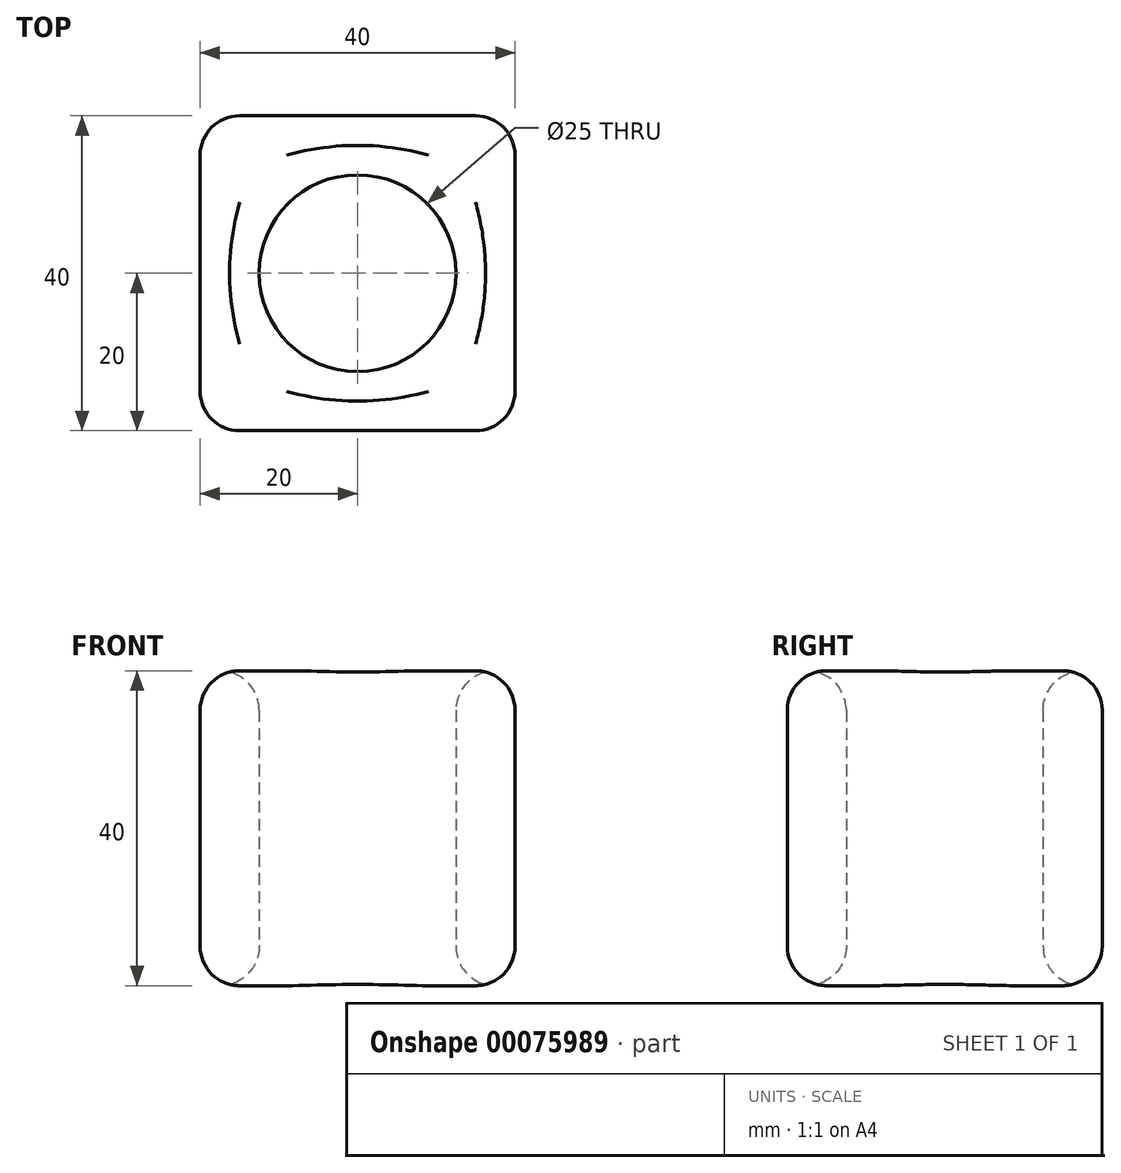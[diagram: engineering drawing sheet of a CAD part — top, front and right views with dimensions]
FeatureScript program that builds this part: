
annotation { "Feature Type Name" : "Feature", "Feature Type Description" : "" }
export const myFeature = defineFeature(function(context is Context, id is Id, definition is map)
    precondition{}
    {
        {
            var Q0;
            Q0=qCreatedBy(makeId("Top.planeOp"),FACE);
            var sketch = newSketch(context, id + "F0", { "sketchPlane" : qUnion([Q0])});
            skLineSegment(sketch, "E0.bottom", {"start": v(20, 20) * mm, "end": v(-20, 20) * mm});
            skLineSegment(sketch, "E0.top", {"start": v(20, -20) * mm, "end": v(-20, -20) * mm});
            skLineSegment(sketch, "E0.left", {"start": v(20, 20) * mm, "end": v(20, -20) * mm});
            skLineSegment(sketch, "E0.right", {"start": v(-20, 20) * mm, "end": v(-20, -20) * mm});
            skPoint(sketch, "E0.middle", {"position": v(0, 0) * mm});
            skCircle(sketch, "E1", {"center": v(0, 0) * mm, "radius": 12.5 * mm});
            skSolve(sketch);
        }
        {
            var Q0;
            Q0=makeQuery(id+"F0.imprint","IMPRINT",FACE,{"disambiguationData":[TD([[makeQuery(id+"F0.imprint","IMPRINT",EDGE,{"derivedFrom":sQuery(id+"F0.wireOp",EDGE,"E0.bottom")}),1.0]])]});
            extrude(context, id + "F1", {"entities" : qUnion([Q0]), "depth" : 20 * mm, "hasSecondDirection" : true, "secondDirectionOppositeDirection" : true, "secondDirectionDepth" : 20 * mm});
        }
        {
            var Q0;
            Q0=makeQuery(id+"F1.opExtrude","CAP_FACE",FACE,{"disambiguationData":[OSD([sQuery(id+"F0.wireOp",EDGE,"E0.bottom"),sQuery(id+"F0.wireOp",EDGE,"E0.top"),sQuery(id+"F0.wireOp",EDGE,"E0.left"),sQuery(id+"F0.wireOp",EDGE,"E0.right"),sQuery(id+"F0.wireOp",EDGE,"E1")])],"isStart":false});
            var Q1;
            Q1=makeQuery(id+"F1.opExtrude","SWEPT_FACE",FACE,{"disambiguationData":[OSD([sQuery(id+"F0.wireOp",EDGE,"E0.bottom")])]});
            var Q2;
            Q2=makeQuery(id+"F1.opExtrude","CAP_FACE",FACE,{"disambiguationData":[OSD([sQuery(id+"F0.wireOp",EDGE,"E0.bottom"),sQuery(id+"F0.wireOp",EDGE,"E0.top"),sQuery(id+"F0.wireOp",EDGE,"E0.left"),sQuery(id+"F0.wireOp",EDGE,"E0.right"),sQuery(id+"F0.wireOp",EDGE,"E1")])],"isStart":true});
            var Q3;
            Q3=makeQuery(id+"F1.opExtrude","SWEPT_FACE",FACE,{"disambiguationData":[OSD([sQuery(id+"F0.wireOp",EDGE,"E0.top")])]});
            var Q4;
            Q4=makeQuery(id+"F1.opExtrude","SWEPT_FACE",FACE,{"disambiguationData":[OSD([sQuery(id+"F0.wireOp",EDGE,"E0.left")])]});
            fillet(context, id + "F2", {"entities" : qUnion([Q0, Q1, Q2, Q3, Q4]), "radius" : 5 * mm, "tangentPropagation" : true, "allowEdgeOverflow" : false});
        }
    });
